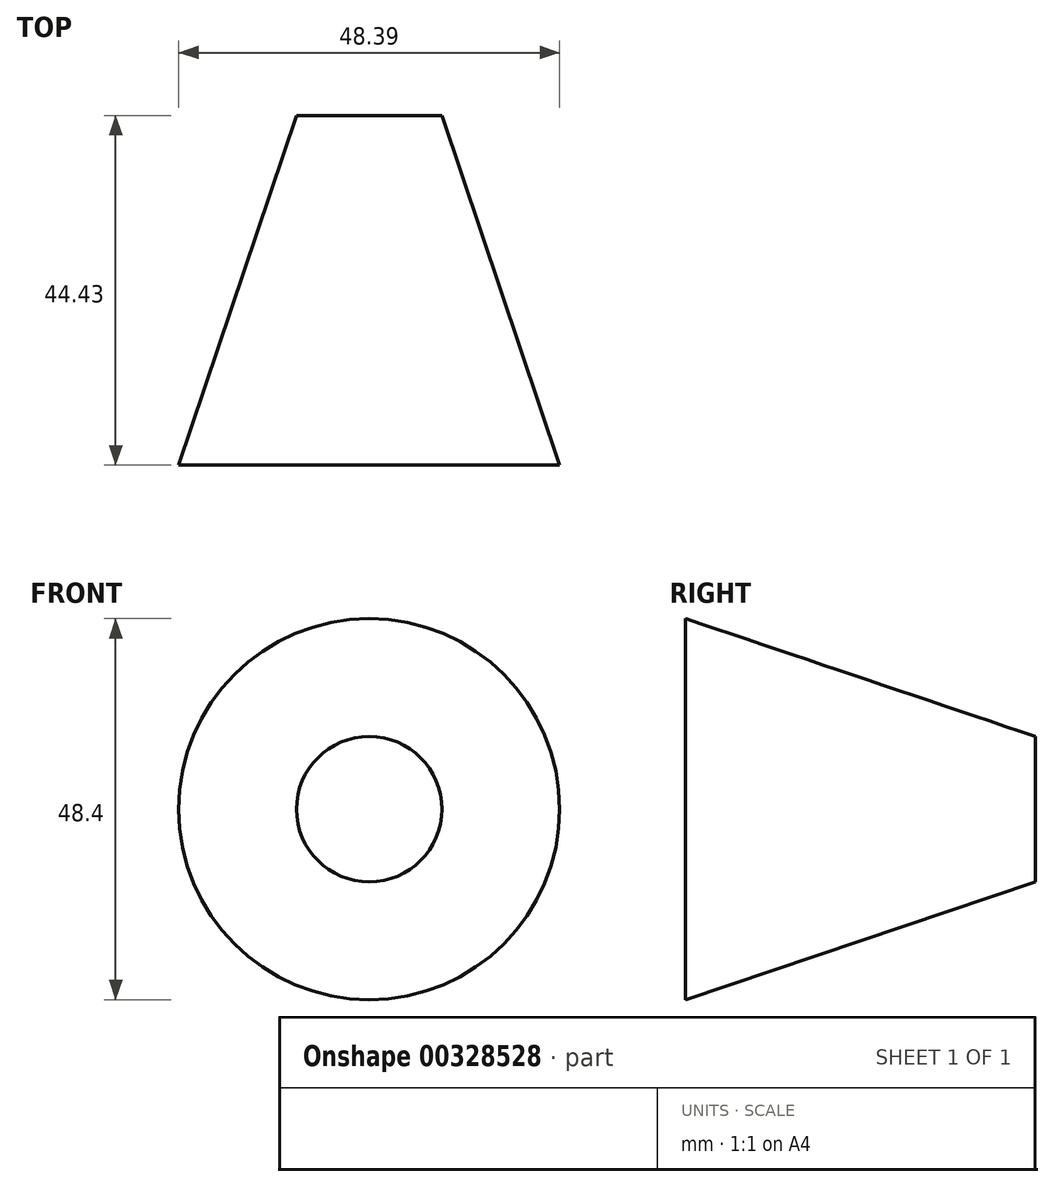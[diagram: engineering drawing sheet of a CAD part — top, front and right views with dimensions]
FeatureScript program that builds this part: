
annotation { "Feature Type Name" : "Feature", "Feature Type Description" : "" }
export const myFeature = defineFeature(function(context is Context, id is Id, definition is map)
    precondition{}
    {
        {
            var Q0;
            Q0=qCreatedBy(makeId("Top.planeOp"),FACE);
            var sketch = newSketch(context, id + "F0", { "sketchPlane" : qUnion([Q0])});
            skLineSegment(sketch, "E0", {"start": v(32.56, 53.01) * mm, "end": v(41.8, 61.37) * mm});
            skLineSegment(sketch, "E1", {"start": v(41.8, 61.37) * mm, "end": v(56.75, 16.94) * mm});
            skLineSegment(sketch, "E2", {"start": v(56.75, 16.94) * mm, "end": v(32.56, 16.94) * mm});
            skLineSegment(sketch, "E3", {"start": v(32.56, 16.94) * mm, "end": v(32.56, 53.01) * mm});
            skSolve(sketch);
        }
        {
            var Q0;
            Q0=sQuery(id+"F0.wireOp",EDGE,"E1");
            var Q1;
            Q1=sQuery(id+"F0.wireOp",EDGE,"E3");
            revolve(context, id + "F1", {"bodyType" : ToolBodyType.SURFACE, "surfaceEntities" : qUnion([Q0]), "axis" : qUnion([Q1]), "revolveType" : RevolveType.FULL});
        }
    });
